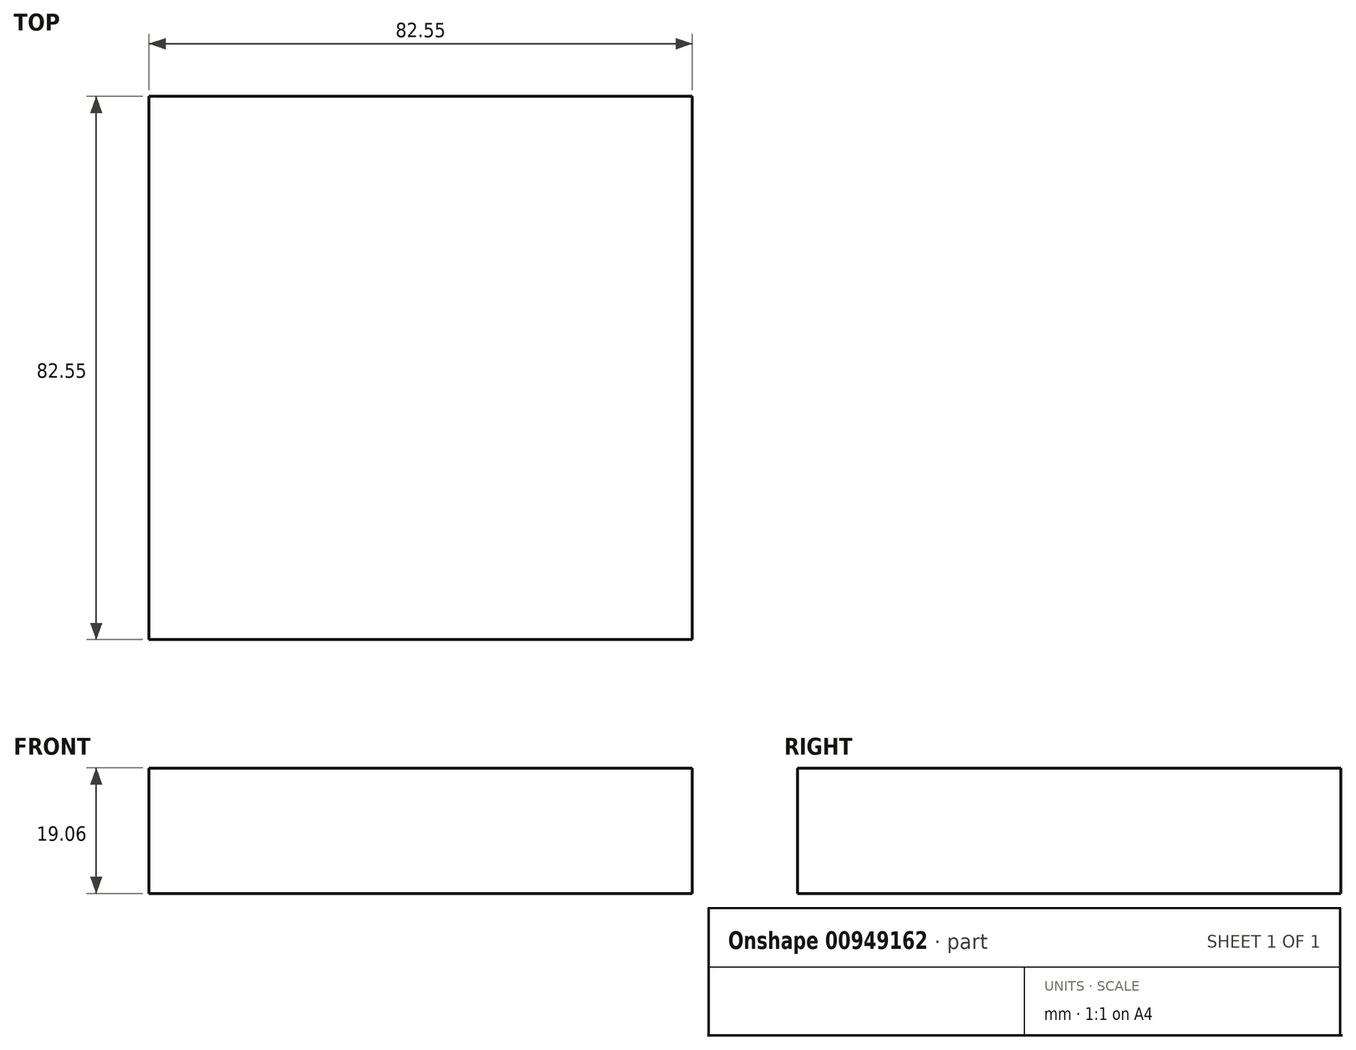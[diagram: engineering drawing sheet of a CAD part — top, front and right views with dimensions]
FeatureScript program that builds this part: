
annotation { "Feature Type Name" : "Feature", "Feature Type Description" : "" }
export const myFeature = defineFeature(function(context is Context, id is Id, definition is map)
    precondition{}
    {
        {
            var Q0;
            Q0=qCreatedBy(makeId("Front.planeOp"),FACE);
            var sketch = newSketch(context, id + "F0", { "sketchPlane" : qUnion([Q0])});
            skLineSegment(sketch, "E0.bottom", {"start": v(41.28, -9.52) * mm, "end": v(-41.27, -9.53) * mm});
            skLineSegment(sketch, "E0.top", {"start": v(41.27, 9.53) * mm, "end": v(-41.27, 9.53) * mm});
            skLineSegment(sketch, "E0.left", {"start": v(41.28, -9.52) * mm, "end": v(41.27, 9.53) * mm});
            skLineSegment(sketch, "E0.right", {"start": v(-41.27, -9.53) * mm, "end": v(-41.27, 9.53) * mm});
            skPoint(sketch, "E0.middle", {"position": v(0, 0) * mm});
            skLineSegment(sketch, "E1", {"start": v(41.27, 9.53) * mm, "end": v(41.27, 27.04) * mm});
            skArc(sketch, "E2", {"start": v(41.27, 27.04) * mm, "mid": v(46.33, 38.66) * mm, "end": v(58.28, 42.88) * mm});
            skLineSegment(sketch, "E3", {"start": v(58.28, 42.88) * mm, "end": v(102.2, 42.88) * mm});
            skLineSegment(sketch, "E4.bottom", {"start": v(122.17, 38.1) * mm, "end": v(71.37, 38.1) * mm});
            skLineSegment(sketch, "E4.top", {"start": v(122.17, 66.68) * mm, "end": v(71.37, 66.68) * mm});
            skLineSegment(sketch, "E4.left", {"start": v(122.17, 38.1) * mm, "end": v(122.17, 66.68) * mm});
            skLineSegment(sketch, "E4.right", {"start": v(71.37, 38.1) * mm, "end": v(71.37, 66.68) * mm});
            skPoint(sketch, "E4.middle", {"position": v(96.77, 52.39) * mm});
            skLineSegment(sketch, "E5.0", {"start": v(58.82, 61.93) * mm, "end": v(102.2, 61.93) * mm});
            skArc(sketch, "E5.1", {"start": v(22.22, 27.04) * mm, "mid": v(33.05, 52.32) * mm, "end": v(58.82, 61.93) * mm});
            skLineSegment(sketch, "E5.2", {"start": v(22.22, 9.53) * mm, "end": v(22.22, 27.04) * mm});
            skLineSegment(sketch, "E6", {"start": v(102.2, 61.93) * mm, "end": v(102.2, 42.88) * mm});
            skLineSegment(sketch, "E7", {"start": v(22.22, 9.53) * mm, "end": v(41.27, 9.53) * mm});
            skFitSpline(sketch, "E8", {"points": [v(-41.27, 9.53) * mm, v(-11.36, 27.63) * mm, v(17.52, 55.1) * mm, v(58.82, 61.93) * mm], "startDerivative": vector(89.74, 37.7) * mm, "endDerivative": vector(126.2, -0.35) * mm});
            skSolve(sketch);
        }
        {
            var Q0;
            Q0=makeQuery(id+"F0.imprint","IMPRINT",FACE,{"disambiguationData":[TD([[makeQuery(id+"F0.imprint","IMPRINT",EDGE,{"derivedFrom":sQuery(id+"F0.wireOp",EDGE,"E0.bottom")}),-1.0]])]});
            extrude(context, id + "F1", {"entities" : qUnion([Q0]), "depth" : 82.55 * mm, "offsetDistance" : 25.4 * mm});
        }
    });
